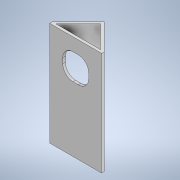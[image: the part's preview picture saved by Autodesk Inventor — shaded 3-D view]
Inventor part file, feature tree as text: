
AUTODESK INVENTOR PART (.ipt)
format: ipt  version: 2020 (Build 240168000, 168)  size: 137,728 bytes
history: native  units: mm
features: extrude x3, sketch x3
ambient origin geometry x8: Origin, YZ Plane, XZ Plane, XY Plane, X Axis, Y Axis, Z Axis, Center Point
bodies: Solid1 (feature_tree)
feature tree (6):
  extrude  "Extrusion1"  Depth=200.0mm
  extrude  "Extrusion2"  TaperAngle=45.0deg  [1 undecoded]
  extrude  "Extrusion6"  Depth=5.0mm
  sketch  "Sketch1"  dims[d0=100.0mm d1=200.0mm]
  sketch  "Sketch2"  dims[d2=5.0mm d3=0.0mm d4=45.0deg]
  sketch  "Sketch6"  dims[d5=5.0mm d6=5.0mm d7=45.0mm d8=0.0mm d21=50.0mm d22=50.0mm d23=20.0mm d24=5.0mm d25=0.0mm]
note: 1 required parameter value undecoded (feature->parameter linkage not recoverable at this tier; creation-order binding heuristic only, values carry confidence <= 0.55)
